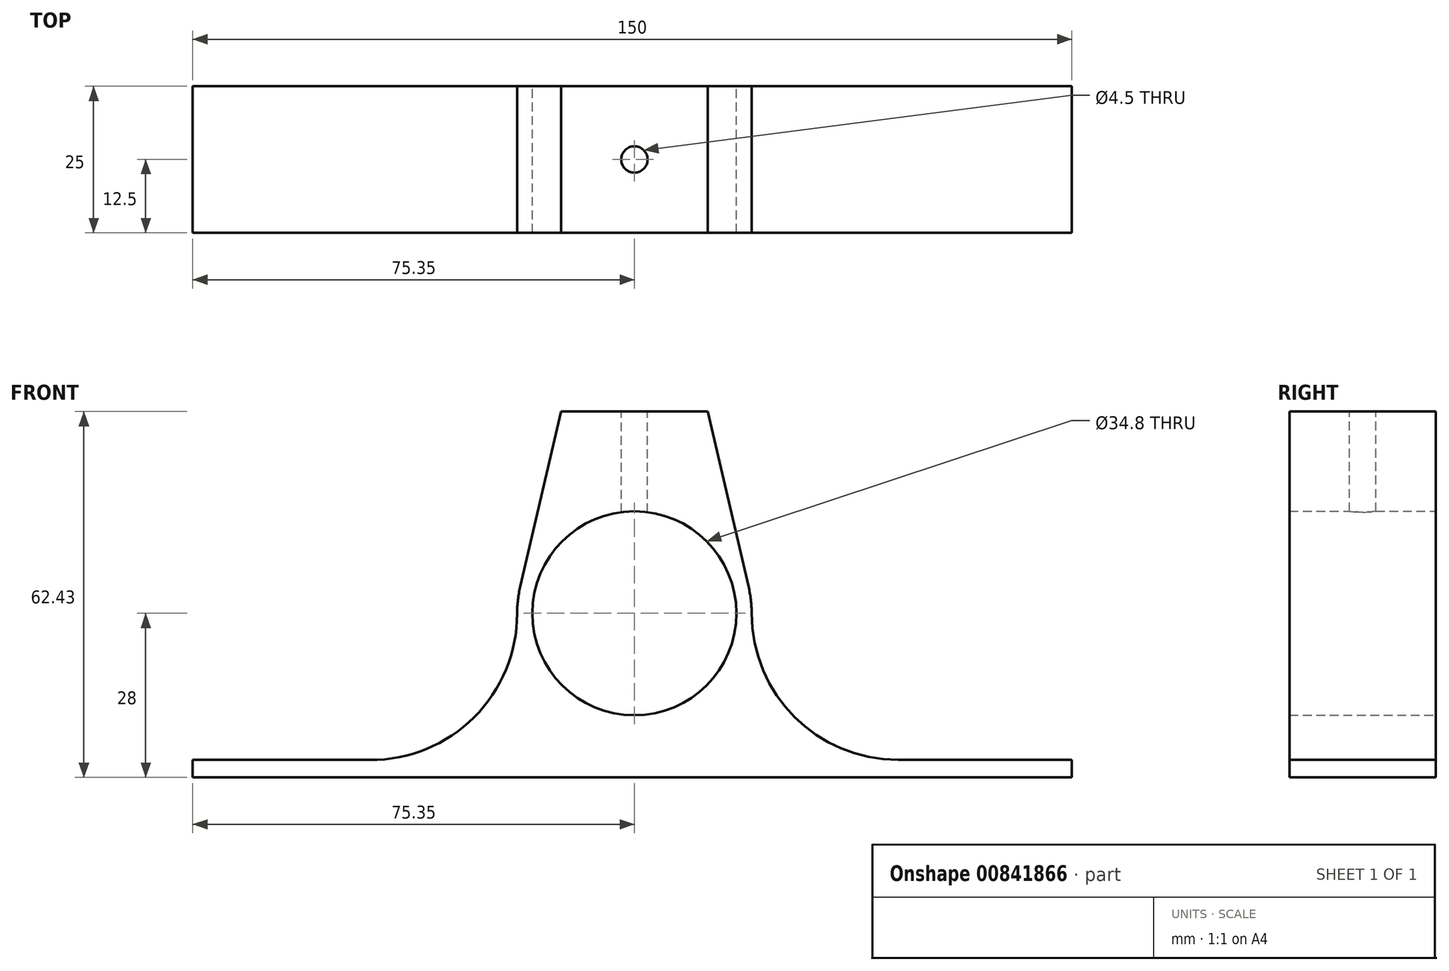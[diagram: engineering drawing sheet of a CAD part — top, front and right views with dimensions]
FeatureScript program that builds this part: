
annotation { "Feature Type Name" : "Feature", "Feature Type Description" : "" }
export const myFeature = defineFeature(function(context is Context, id is Id, definition is map)
    precondition{}
    {
        {
            var Q0;
            Q0=qCreatedBy(makeId("Front.planeOp"),FACE);
            var sketch = newSketch(context, id + "F0", { "sketchPlane" : qUnion([Q0])});
            skCircle(sketch, "E0", {"center": v(0, 0) * mm, "radius": 20 * mm});
            skLineSegment(sketch, "E1.bottom", {"start": v(-50.35, -25) * mm, "end": v(-75.35, -25) * mm});
            skPoint(sketch, "E1.middle", {"position": v(0, -30) * mm});
            skPoint(sketch, "E2.newPointB", {"position": v(74.65, -25) * mm});
            skLineSegment(sketch, "E3", {"start": v(50.35, -25) * mm, "end": v(75.35, -25) * mm});
            skCircle(sketch, "E4", {"center": v(0, 0) * mm, "radius": 17.4 * mm});
            skLineSegment(sketch, "E5", {"start": v(-20, 0) * mm, "end": v(-20, -0.02) * mm});
            skLineSegment(sketch, "E6", {"start": v(-45.1, -25.02) * mm, "end": v(-50.35, -25) * mm});
            skLineSegment(sketch, "E7", {"start": v(20, 0) * mm, "end": v(20, 0) * mm});
            skLineSegment(sketch, "E8", {"start": v(45, -25) * mm, "end": v(50.35, -25) * mm});
            skPoint(sketch, "E9.visualSharp", {"position": v(20, -25) * mm});
            skArc(sketch, "E9.filletArc", {"start": v(20, 0) * mm, "mid": v(27.32, -17.68) * mm, "end": v(45, -25) * mm});
            skPoint(sketch, "E10.visualSharp", {"position": v(-20, -25.12) * mm});
            skArc(sketch, "E10.filletArc", {"start": v(-45.1, -25.02) * mm, "mid": v(-27.36, -17.74) * mm, "end": v(-20, -0.02) * mm});
            skLineSegment(sketch, "E11", {"start": v(-75.35, -25) * mm, "end": v(-75.35, -28) * mm});
            skLineSegment(sketch, "E12", {"start": v(-75.35, -28) * mm, "end": v(74.65, -28) * mm});
            skLineSegment(sketch, "E13", {"start": v(74.65, -28) * mm, "end": v(74.65, -25) * mm});
            skLineSegment(sketch, "E14", {"start": v(0, 34.43) * mm, "end": v(-12.5, 34.43) * mm});
            skLineSegment(sketch, "E15.MirrorCS", {"start": v(0, 34.43) * mm, "end": v(12.5, 34.43) * mm});
            skLineSegment(sketch, "E16", {"start": v(-12.5, 34.43) * mm, "end": v(-19.48, 4.55) * mm});
            skLineSegment(sketch, "E17", {"start": v(12.5, 34.43) * mm, "end": v(19.48, 4.55) * mm});
            skSolve(sketch);
        }
        {
            var Q0;
            Q0=makeQuery(id+"F0.imprint","IMPRINT",FACE,{"disambiguationData":[TD([[makeQuery(id+"F0.imprint","IMPRINT",EDGE,{"derivedFrom":sQuery(id+"F0.wireOp",EDGE,"E14")}),1.0]])]});
            var Q1;
            Q1=makeQuery(id+"F0.imprint","IMPRINT",FACE,{"disambiguationData":[TD([[makeQuery(id+"F0.imprint","IMPRINT",EDGE,{"derivedFrom":sQuery(id+"F0.wireOp",EDGE,"E4")}),-1.0]])]});
            var Q2;
            Q2=makeQuery(id+"F0.imprint","IMPRINT",FACE,{"disambiguationData":[TD([[makeQuery(id+"F0.imprint","IMPRINT",EDGE,{"derivedFrom":sQuery(id+"F0.wireOp",EDGE,"E1.bottom")}),1.0]])]});
            extrude(context, id + "F1", {"entities" : qUnion([Q0, Q1, Q2]), "depth" : 25 * mm, "offsetDistance" : 25 * mm});
        }
        {
            var Q0;
            Q0=makeQuery(id+"F1.opExtrude","SWEPT_FACE",FACE,{"disambiguationData":[OSD([sQuery(id+"F0.wireOp",EDGE,"E14"),sQuery(id+"F0.wireOp",EDGE,"E15.MirrorCS")])]});
            var sketch = newSketch(context, id + "F2", { "sketchPlane" : qUnion([Q0])});
            skLineSegment(sketch, "E18", {"start": v(0, 0) * mm, "end": v(0, -12.5) * mm});
            skCircle(sketch, "E19", {"center": v(0, -12.5) * mm, "radius": 2.25 * mm});
            skSolve(sketch);
        }
        {
            var Q0;
            Q0=makeQuery(id+"F2.imprint","IMPRINT",FACE,{"disambiguationData":[TD([[makeQuery(id+"F2.imprint","IMPRINT",EDGE,{"derivedFrom":sQuery(id+"F2.wireOp",EDGE,"E19")}),1.0]])]});
            extrude(context, id + "F3", {"entities" : qUnion([Q0]), "operationType" : NewBodyOperationType.REMOVE, "oppositeDirection" : true, "depth" : 50 * mm, "offsetDistance" : 25 * mm});
        }
    });
